# Revit family: 02-66-003 DN50-250
name_source: partatom
category: Plumbing Fixtures
units: mm (PartAtom-declared; Revit-internal decimal feet)

## family parameters
Always vertical = Yes
Cut with Voids When Loaded = No
Maintain Annotation Orientation = No
Part Type = Normal
Room Calculation Point = No
Round Connector Dimension = Use Diameter
Shared = No
Work Plane-Based = No

## types (8) — shared parameters
1 = 1 mm  [stored 0.00328084 ft]
10 = 10 mm  [stored 0.0328084 ft]
5 = 5 mm  [stored 0.0164042 ft]
DN050_PN10/16 = 02-050-66-014
DN080_PN10/16 = 02-080-66-014
DN100_PN10/16 = 02-100-66-014
DN125_PN10/16 = 02-125-66-014
DN150_PN10/16 = 02-150-66-014
DN200_PN10 = 02-200-66-004
DN200_PN16 = 02-200-66-014
DN250_PN10 = 02-250-66-004
Description_ = AVK GATE VALVE, FLANGED, PN10/16
Search_table = 02-66-003 DN50-250
URL_product_pages = https://www.avkvalves.com
zero-valued in all types: Default Elevation

## per-type parameters (varying)
- DN050_PN10/16: Body_Arc=150 mm; Body_FL_L=67 mm; Body_FL_R=20 mm  [stored 0.0656168 ft]; Body_FL_T=10 mm  [stored 0.0328084 ft]; Body_FL_W=46 mm; Body_FL_arc=200 mm; Body_FL_rib_dim=238 mm; Body_FL_rib_dim1=106 mm; Body_H=110 mm; Body_L=52 mm; Body_R=10 mm  [stored 0.0328084 ft]; Body_T=6 mm  [stored 0.019685 ft]; Body_W=35 mm  [stored 0.114829 ft]; Body_bottom=22 mm  [stored 0.0721785 ft]; Bonnet_L=47 mm; Bonnet_d1=28 mm  [stored 0.0918635 ft]; Bonnet_d2=18 mm  [stored 0.0590551 ft]; Bonnet_dim1=38 mm  [stored 0.124672 ft]; Bonnet_dim2=32 mm  [stored 0.104987 ft]; Bonnet_dim3=23 mm  [stored 0.0754593 ft]; Bore_R=25 mm  [stored 0.082021 ft]; D=180 mm; D-F2=72 mm; D1=72 mm; DN=50 mm; Dh=125 mm; Ds=19 mm  [stored 0.062336 ft]; F=7 mm  [stored 0.0229659 ft]; F1=9 mm  [stored 0.0295276 ft]; F2=29 mm  [stored 0.0951444 ft]; FL_R=83 mm; FL_T=19 mm  [stored 0.062336 ft]; H=268 mm; H3=350 mm; H3-H=82 mm; Handwheel_D1=12 mm  [stored 0.0393701 ft]; Handwheel_D2=4 mm  [stored 0.0131234 ft]; Handwheel_R=15 mm  [stored 0.0492126 ft]; Handwheel_T=20 mm  [stored 0.0656168 ft]; L=250 mm; L1=88 mm; RIB_L=82 mm; RIB_L1=54 mm; RIB_T=6 mm  [stored 0.019685 ft]; Raised_R=49 mm; Raised_dis=3 mm  [stored 0.00984252 ft]; Rib1_H=60 mm; Rib1_L=80 mm; Rib1_R=20 mm  [stored 0.0656168 ft]; Rib1_T=5 mm  [stored 0.0164042 ft]; Rib1_W=50 mm; Rib2_H=60 mm; Rib2_L=80 mm; Rib2_W=50 mm; Rib3_H=60 mm; Rib3_L=80 mm; Rib3_W=50 mm; Rib4_H=60 mm; Rib4_L=80 mm; Rib4_W=50 mm; Rib5_H=60 mm; Rib5_L=80 mm; Rib5_W=50 mm; Rib_T=16 mm  [stored 0.0524934 ft]; Slant=36 mm  [stored 0.11811 ft]; Stem=67 mm; Stem_D=15 mm  [stored 0.0492126 ft]; Stem_D2=11 mm  [stored 0.0360892 ft]; Stem_H=201 mm; Stem_shaft=18 mm  [stored 0.0590551 ft]; Sweep _cut=2 mm  [stored 0.00656168 ft]; W=83 mm; Wedge_L=30 mm  [stored 0.0984252 ft]; handwheel=18 mm  [stored 0.0590551 ft]; handwheel_T=8 mm  [stored 0.0262467 ft]; logo_H=55 mm; stem1=12 mm  [stored 0.0393701 ft]; stem_t=2 mm  [stored 0.00656168 ft]
- DN080_PN10/16: Body_Arc=212 mm; Body_FL_L=86 mm; Body_FL_R=20 mm  [stored 0.0656168 ft]; Body_FL_T=12 mm  [stored 0.0393701 ft]; Body_FL_W=48 mm; Body_FL_arc=775 mm; Body_FL_rib_dim=294 mm; Body_FL_rib_dim1=121 mm; Body_H=108 mm; Body_L=72 mm; Body_R=16 mm  [stored 0.0524934 ft]; Body_T=7 mm  [stored 0.0229659 ft]; Body_W=35 mm  [stored 0.114829 ft]; Body_bottom=42 mm  [stored 0.137795 ft]; Bonnet_L=65 mm; Bonnet_d1=28 mm  [stored 0.0918635 ft]; Bonnet_d2=18 mm  [stored 0.0590551 ft]; Bonnet_dim1=48 mm; Bonnet_dim2=34 mm  [stored 0.111549 ft]; Bonnet_dim3=29 mm  [stored 0.0951444 ft]; Bore_R=40 mm  [stored 0.131234 ft]; D=225 mm; D-F2=91 mm; D1=90 mm; DN=80 mm; Dh=160 mm; Ds=19 mm  [stored 0.062336 ft]; F=9 mm  [stored 0.0295276 ft]; F1=12 mm  [stored 0.0393701 ft]; F2=34 mm  [stored 0.111549 ft]; FL_R=100 mm; FL_T=19 mm  [stored 0.062336 ft]; H=324 mm; H3=424 mm; H3-H=100 mm; Handwheel_D1=14 mm  [stored 0.0459318 ft]; Handwheel_D2=5 mm  [stored 0.0164042 ft]; Handwheel_R=17 mm  [stored 0.0557743 ft]; Handwheel_T=24 mm  [stored 0.0787402 ft]; L=280 mm; L1=98 mm; RIB_L=99 mm; RIB_L1=65 mm; RIB_T=6 mm  [stored 0.019685 ft]; Raised_R=66 mm; Raised_dis=3 mm  [stored 0.00984252 ft]; Rib1_H=58 mm; Rib1_L=120 mm; Rib1_R=20 mm  [stored 0.0656168 ft]; Rib1_T=5 mm  [stored 0.0164042 ft]; Rib1_W=60 mm; Rib2_H=58 mm; Rib2_L=120 mm; Rib2_W=60 mm; Rib3_H=58 mm; Rib3_L=120 mm; Rib3_W=60 mm; Rib4_H=58 mm; Rib4_L=120 mm; Rib4_W=60 mm; Rib5_H=58 mm; Rib5_L=120 mm; Rib5_W=60 mm; Rib_T=16 mm  [stored 0.0524934 ft]; Slant=54 mm; Stem=81 mm; Stem_D=19 mm  [stored 0.062336 ft]; Stem_D2=14 mm  [stored 0.0459318 ft]; Stem_H=243 mm; Stem_shaft=23 mm  [stored 0.0754593 ft]; Sweep _cut=2 mm  [stored 0.00656168 ft]; W=100 mm; Wedge_L=30 mm  [stored 0.0984252 ft]; handwheel=22 mm  [stored 0.0721785 ft]; handwheel_T=8 mm  [stored 0.0262467 ft]; logo_H=54 mm; stem1=16 mm  [stored 0.0524934 ft]; stem_t=3 mm  [stored 0.00984252 ft]
- DN100_PN10/16: Body_Arc=220 mm; Body_FL_L=96 mm; Body_FL_R=20 mm  [stored 0.0656168 ft]; Body_FL_T=13 mm; Body_FL_W=53 mm; Body_FL_arc=400 mm; Body_FL_rib_dim=332 mm; Body_FL_rib_dim1=132 mm; Body_H=122 mm; Body_L=82 mm; Body_R=16 mm  [stored 0.0524934 ft]; Body_T=6 mm  [stored 0.019685 ft]; Body_W=38 mm  [stored 0.124672 ft]; Body_bottom=52 mm; Bonnet_L=74 mm; Bonnet_d1=30 mm  [stored 0.0984252 ft]; Bonnet_d2=19 mm  [stored 0.062336 ft]; Bonnet_dim1=48 mm; Bonnet_dim2=37 mm; Bonnet_dim3=29 mm  [stored 0.0951444 ft]; Bore_R=50 mm; D=280 mm; D-F2=118 mm; D1=112 mm; DN=100 mm; Dh=180 mm; Ds=19 mm  [stored 0.062336 ft]; F=10 mm  [stored 0.0328084 ft]; F1=12 mm  [stored 0.0393701 ft]; F2=34 mm  [stored 0.111549 ft]; FL_R=110 mm; FL_T=18 mm  [stored 0.0590551 ft]; H=362 mm; H3=472 mm; H3-H=110 mm; Handwheel_D1=14 mm  [stored 0.0459318 ft]; Handwheel_D2=5 mm  [stored 0.0164042 ft]; Handwheel_R=17 mm  [stored 0.0557743 ft]; Handwheel_T=24 mm  [stored 0.0787402 ft]; L=300 mm; L1=105 mm; RIB_L=109 mm; RIB_L1=72 mm; RIB_T=6 mm  [stored 0.019685 ft]; Raised_R=77 mm; Raised_dis=3 mm  [stored 0.00984252 ft]; Rib1_H=72 mm; Rib1_L=120 mm; Rib1_R=20 mm  [stored 0.0656168 ft]; Rib1_T=5 mm  [stored 0.0164042 ft]; Rib1_W=60 mm; Rib2_H=72 mm; Rib2_L=120 mm; Rib2_W=60 mm; Rib3_H=72 mm; Rib3_L=120 mm; Rib3_W=60 mm; Rib4_H=72 mm; Rib4_L=120 mm; Rib4_W=60 mm; Rib5_H=72 mm; Rib5_L=120 mm; Rib5_W=60 mm; Rib_T=15 mm  [stored 0.0492126 ft]; Slant=62 mm; Stem=91 mm; Stem_D=19 mm  [stored 0.062336 ft]; Stem_D2=14 mm  [stored 0.0459318 ft]; Stem_H=272 mm; Stem_shaft=28 mm  [stored 0.0918635 ft]; Sweep _cut=2 mm  [stored 0.00656168 ft]; W=110 mm; Wedge_L=32 mm  [stored 0.104987 ft]; handwheel=22 mm  [stored 0.0721785 ft]; handwheel_T=10 mm  [stored 0.0328084 ft]; logo_H=61 mm; stem1=16 mm  [stored 0.0524934 ft]; stem_t=3 mm  [stored 0.00984252 ft]
- DN125_PN10/16: Body_Arc=300 mm; Body_FL_L=110 mm; Body_FL_R=20 mm  [stored 0.0656168 ft]; Body_FL_T=13 mm; Body_FL_W=53 mm; Body_FL_arc=450 mm; Body_FL_rib_dim=375 mm; Body_FL_rib_dim1=145 mm; Body_H=145 mm; Body_L=100 mm; Body_R=16 mm  [stored 0.0524934 ft]; Body_T=6 mm  [stored 0.019685 ft]; Body_W=43 mm  [stored 0.141076 ft]; Body_bottom=70 mm; Bonnet_L=90 mm; Bonnet_d1=34 mm  [stored 0.111549 ft]; Bonnet_d2=22 mm  [stored 0.0721785 ft]; Bonnet_dim1=48 mm; Bonnet_dim2=37 mm; Bonnet_dim3=29 mm  [stored 0.0951444 ft]; Bore_R=63 mm; D=320 mm; D-F2=135 mm; D1=128 mm; DN=125 mm; Dh=190 mm; Ds=20 mm  [stored 0.0656168 ft]; F=10 mm  [stored 0.0328084 ft]; F1=12 mm  [stored 0.0393701 ft]; F2=34 mm  [stored 0.111549 ft]; FL_R=135 mm; FL_T=18 mm  [stored 0.0590551 ft]; H=405 mm; H3=530 mm; H3-H=125 mm; Handwheel_D1=14 mm  [stored 0.0459318 ft]; Handwheel_D2=5 mm  [stored 0.0164042 ft]; Handwheel_R=17 mm  [stored 0.0557743 ft]; Handwheel_T=26 mm; L=325 mm; L1=114 mm; RIB_L=124 mm; RIB_L1=81 mm; RIB_T=6 mm  [stored 0.019685 ft]; Raised_R=80 mm; Raised_dis=3 mm  [stored 0.00984252 ft]; Rib1_H=90 mm; Rib1_L=120 mm; Rib1_R=20 mm  [stored 0.0656168 ft]; Rib1_T=5 mm  [stored 0.0164042 ft]; Rib1_W=60 mm; Rib2_H=90 mm; Rib2_L=120 mm; Rib2_W=60 mm; Rib3_H=100 mm; Rib3_L=120 mm; Rib3_W=60 mm; Rib4_H=90 mm; Rib4_L=120 mm; Rib4_W=60 mm; Rib5_H=90 mm; Rib5_L=120 mm; Rib5_W=60 mm; Rib_T=15 mm  [stored 0.0492126 ft]; Slant=75 mm; Stem=101 mm; Stem_D=19 mm  [stored 0.062336 ft]; Stem_D2=14 mm  [stored 0.0459318 ft]; Stem_H=304 mm; Stem_shaft=32 mm  [stored 0.104987 ft]; Sweep _cut=2 mm  [stored 0.00656168 ft]; W=125 mm; Wedge_L=37 mm; handwheel=25 mm  [stored 0.082021 ft]; handwheel_T=10 mm  [stored 0.0328084 ft]; logo_H=73 mm; stem1=16 mm  [stored 0.0524934 ft]; stem_t=3 mm  [stored 0.00984252 ft]
- DN150_PN10/16: Body_Arc=400 mm; Body_FL_L=136 mm; Body_FL_R=20 mm  [stored 0.0656168 ft]; Body_FL_T=13 mm; Body_FL_W=75 mm; Body_FL_arc=300 mm; Body_FL_rib_dim=447 mm; Body_FL_rib_dim1=157 mm; Body_H=172 mm; Body_L=122 mm; Body_R=16 mm  [stored 0.0524934 ft]; Body_T=6 mm  [stored 0.019685 ft]; Body_W=48 mm; Body_bottom=92 mm; Bonnet_L=110 mm; Bonnet_d1=38 mm  [stored 0.124672 ft]; Bonnet_d2=24 mm  [stored 0.0787402 ft]; Bonnet_dim1=46 mm; Bonnet_dim2=53 mm; Bonnet_dim3=28 mm  [stored 0.0918635 ft]; Bore_R=75 mm; D=320 mm; D-F2=132 mm; D1=128 mm; DN=150 mm; Dh=240 mm; Ds=23 mm  [stored 0.0754593 ft]; F=10 mm  [stored 0.0328084 ft]; F1=11 mm  [stored 0.0360892 ft]; F2=34 mm  [stored 0.111549 ft]; FL_R=143 mm; FL_T=18 mm  [stored 0.0590551 ft]; H=477 mm; H3=620 mm; H3-H=143 mm; Handwheel_D1=14 mm  [stored 0.0459318 ft]; Handwheel_D2=5 mm  [stored 0.0164042 ft]; Handwheel_R=17 mm  [stored 0.0557743 ft]; Handwheel_T=28 mm  [stored 0.0918635 ft]; L=350 mm; L1=123 mm; RIB_L=142 mm; RIB_L1=93 mm; RIB_T=6 mm  [stored 0.019685 ft]; Raised_R=106 mm; Raised_dis=3 mm  [stored 0.00984252 ft]; Rib1_H=122 mm; Rib1_L=120 mm; Rib1_R=20 mm  [stored 0.0656168 ft]; Rib1_T=5 mm  [stored 0.0164042 ft]; Rib1_W=60 mm; Rib2_H=122 mm; Rib2_L=120 mm; Rib2_W=60 mm; Rib3_H=122 mm; Rib3_L=120 mm; Rib3_W=60 mm; Rib4_H=122 mm; Rib4_L=120 mm; Rib4_W=60 mm; Rib5_H=122 mm; Rib5_L=120 mm; Rib5_W=60 mm; Rib_T=15 mm  [stored 0.0492126 ft]; Slant=87 mm; Stem=119 mm; Stem_D=18 mm  [stored 0.0590551 ft]; Stem_D2=13 mm; Stem_H=358 mm; Stem_shaft=32 mm  [stored 0.104987 ft]; Sweep _cut=2 mm  [stored 0.00656168 ft]; W=143 mm; Wedge_L=41 mm; handwheel=28 mm  [stored 0.0918635 ft]; handwheel_T=15 mm  [stored 0.0492126 ft]; logo_H=86 mm; stem1=15 mm  [stored 0.0492126 ft]; stem_t=3 mm  [stored 0.00984252 ft]
- DN200_PN10: Body_Arc=500 mm; Body_FL_L=166 mm; Body_FL_R=25 mm  [stored 0.082021 ft]; Body_FL_T=15 mm  [stored 0.0492126 ft]; Body_FL_W=85 mm; Body_FL_arc=450 mm; Body_FL_rib_dim=563 mm; Body_FL_rib_dim1=180 mm; Body_H=220 mm; Body_L=157 mm; Body_R=20 mm  [stored 0.0656168 ft]; Body_T=7 mm  [stored 0.0229659 ft]; Body_W=55 mm; Body_bottom=127 mm; Bonnet_L=141 mm; Bonnet_d1=44 mm  [stored 0.144357 ft]; Bonnet_d2=28 mm  [stored 0.0918635 ft]; Bonnet_dim1=59 mm; Bonnet_dim2=60 mm; Bonnet_dim3=35 mm  [stored 0.114829 ft]; Bore_R=100 mm; D=360 mm; D-F2=150 mm; D1=144 mm; DN=200 mm; Dh=295 mm; Ds=23 mm  [stored 0.0754593 ft]; F=12 mm  [stored 0.0393701 ft]; F1=14 mm  [stored 0.0459318 ft]; F2=34 mm  [stored 0.111549 ft]; FL_R=170 mm; FL_T=20 mm  [stored 0.0656168 ft]; H=593 mm; H3=763 mm; H3-H=170 mm; Handwheel_D1=14 mm  [stored 0.0459318 ft]; Handwheel_D2=5 mm  [stored 0.0164042 ft]; Handwheel_R=17 mm  [stored 0.0557743 ft]; Handwheel_T=30 mm  [stored 0.0984252 ft]; L=400 mm; L1=140 mm; RIB_L=169 mm; RIB_L1=111 mm; RIB_T=6 mm  [stored 0.019685 ft]; Raised_R=132 mm; Raised_dis=3 mm  [stored 0.00984252 ft]; Rib1_H=170 mm; Rib1_L=120 mm; Rib1_R=20 mm  [stored 0.0656168 ft]; Rib1_T=5 mm  [stored 0.0164042 ft]; Rib1_W=60 mm; Rib2_H=170 mm; Rib2_L=120 mm; Rib2_W=60 mm; Rib3_H=170 mm; Rib3_L=120 mm; Rib3_W=60 mm; Rib4_H=170 mm; Rib4_L=120 mm; Rib4_W=60 mm; Rib5_H=170 mm; Rib5_L=120 mm; Rib5_W=60 mm; Rib_T=17 mm  [stored 0.0557743 ft]; Slant=114 mm; Stem=148 mm; Stem_D=23 mm  [stored 0.0754593 ft]; Stem_D2=17 mm  [stored 0.0557743 ft]; Stem_H=445 mm; Stem_shaft=36 mm  [stored 0.11811 ft]; Sweep _cut=3 mm  [stored 0.00984252 ft]; W=170 mm; Wedge_L=47 mm; handwheel=30 mm  [stored 0.0984252 ft]; handwheel_T=17 mm  [stored 0.0557743 ft]; logo_H=110 mm; stem1=19 mm  [stored 0.062336 ft]; stem_t=4 mm  [stored 0.0131234 ft]
- DN200_PN16: Body_Arc=500 mm; Body_FL_L=166 mm; Body_FL_R=25 mm  [stored 0.082021 ft]; Body_FL_T=15 mm  [stored 0.0492126 ft]; Body_FL_W=85 mm; Body_FL_arc=450 mm; Body_FL_rib_dim=563 mm; Body_FL_rib_dim1=180 mm; Body_H=220 mm; Body_L=157 mm; Body_R=20 mm  [stored 0.0656168 ft]; Body_T=7 mm  [stored 0.0229659 ft]; Body_W=55 mm; Body_bottom=127 mm; Bonnet_L=141 mm; Bonnet_d1=44 mm  [stored 0.144357 ft]; Bonnet_d2=28 mm  [stored 0.0918635 ft]; Bonnet_dim1=59 mm; Bonnet_dim2=60 mm; Bonnet_dim3=35 mm  [stored 0.114829 ft]; Bore_R=100 mm; D=360 mm; D-F2=150 mm; D1=144 mm; DN=200 mm; Dh=295 mm; Ds=23 mm  [stored 0.0754593 ft]; F=12 mm  [stored 0.0393701 ft]; F1=14 mm  [stored 0.0459318 ft]; F2=34 mm  [stored 0.111549 ft]; FL_R=170 mm; FL_T=20 mm  [stored 0.0656168 ft]; H=593 mm; H3=763 mm; H3-H=170 mm; Handwheel_D1=14 mm  [stored 0.0459318 ft]; Handwheel_D2=5 mm  [stored 0.0164042 ft]; Handwheel_R=17 mm  [stored 0.0557743 ft]; Handwheel_T=30 mm  [stored 0.0984252 ft]; L=400 mm; L1=140 mm; RIB_L=169 mm; RIB_L1=111 mm; RIB_T=6 mm  [stored 0.019685 ft]; Raised_R=132 mm; Raised_dis=3 mm  [stored 0.00984252 ft]; Rib1_H=170 mm; Rib1_L=120 mm; Rib1_R=20 mm  [stored 0.0656168 ft]; Rib1_T=5 mm  [stored 0.0164042 ft]; Rib1_W=60 mm; Rib2_H=170 mm; Rib2_L=120 mm; Rib2_W=60 mm; Rib3_H=170 mm; Rib3_L=120 mm; Rib3_W=60 mm; Rib4_H=170 mm; Rib4_L=120 mm; Rib4_W=60 mm; Rib5_H=170 mm; Rib5_L=120 mm; Rib5_W=60 mm; Rib_T=17 mm  [stored 0.0557743 ft]; Slant=114 mm; Stem=148 mm; Stem_D=23 mm  [stored 0.0754593 ft]; Stem_D2=17 mm  [stored 0.0557743 ft]; Stem_H=445 mm; Stem_shaft=36 mm  [stored 0.11811 ft]; Sweep _cut=3 mm  [stored 0.00984252 ft]; W=170 mm; Wedge_L=47 mm; handwheel=30 mm  [stored 0.0984252 ft]; handwheel_T=17 mm  [stored 0.0557743 ft]; logo_H=110 mm; stem1=19 mm  [stored 0.062336 ft]; stem_t=4 mm  [stored 0.0131234 ft]
- DN250_PN10: Body_Arc=900 mm; Body_FL_L=211 mm; Body_FL_R=25 mm  [stored 0.082021 ft]; Body_FL_T=15 mm  [stored 0.0492126 ft]; Body_FL_W=107 mm; Body_FL_arc=1000 mm; Body_FL_rib_dim=665 mm; Body_FL_rib_dim1=205 mm; Body_H=285 mm; Body_L=196 mm; Body_R=25 mm  [stored 0.082021 ft]; Body_T=9 mm  [stored 0.0295276 ft]; Body_W=73 mm; Body_bottom=166 mm; Bonnet_L=176 mm; Bonnet_d1=58 mm; Bonnet_d2=36 mm  [stored 0.11811 ft]; Bonnet_dim1=76 mm; Bonnet_dim2=75 mm; Bonnet_dim3=45 mm; Bore_R=125 mm; D=500 mm; D-F2=220 mm; D1=200 mm; DN=250 mm; Dh=350 mm; Ds=23 mm  [stored 0.0754593 ft]; F=14 mm  [stored 0.0459318 ft]; F1=18 mm  [stored 0.0590551 ft]; F2=47 mm; FL_R=200 mm; FL_T=20 mm  [stored 0.0656168 ft]; H=695 mm; H3=895 mm; H3-H=200 mm; Handwheel_D1=19 mm  [stored 0.062336 ft]; Handwheel_D2=7 mm  [stored 0.0229659 ft]; Handwheel_R=24 mm  [stored 0.0787402 ft]; Handwheel_T=32 mm  [stored 0.104987 ft]; L=450 mm; L1=158 mm; RIB_L=199 mm; RIB_L1=130 mm; RIB_T=4 mm  [stored 0.0131234 ft]; Raised_R=160 mm; Raised_dis=2 mm  [stored 0.00656168 ft]; Rib1_H=200 mm; Rib1_L=420 mm; Rib1_R=60 mm; Rib1_T=8 mm  [stored 0.0262467 ft]; Rib1_W=195 mm; Rib2_H=160 mm; Rib2_L=200 mm; Rib2_W=140 mm; Rib3_H=220 mm; Rib3_L=200 mm; Rib3_W=140 mm; Rib4_H=180 mm; Rib4_L=200 mm; Rib4_W=140 mm; Rib5_H=220 mm; Rib5_L=200 mm; Rib5_W=140 mm; Rib_T=18 mm  [stored 0.0590551 ft]; Slant=142 mm; Stem=174 mm; Stem_D=29 mm  [stored 0.0951444 ft]; Stem_D2=22 mm  [stored 0.0721785 ft]; Stem_H=521 mm; Stem_shaft=50 mm; Sweep _cut=3 mm  [stored 0.00984252 ft]; W=200 mm; Wedge_L=62 mm; handwheel=30 mm  [stored 0.0984252 ft]; handwheel_T=17 mm  [stored 0.0557743 ft]; logo_H=143 mm; stem1=24 mm  [stored 0.0787402 ft]; stem_t=5 mm  [stored 0.0164042 ft]

note: [stored X ft] marks values corroborated as IEEE doubles in the binary element streams (Revit-internal decimal feet)

## geometry (parser evidence)
native form markers: Sweep x6
no freeform markers — native parametric forms only
